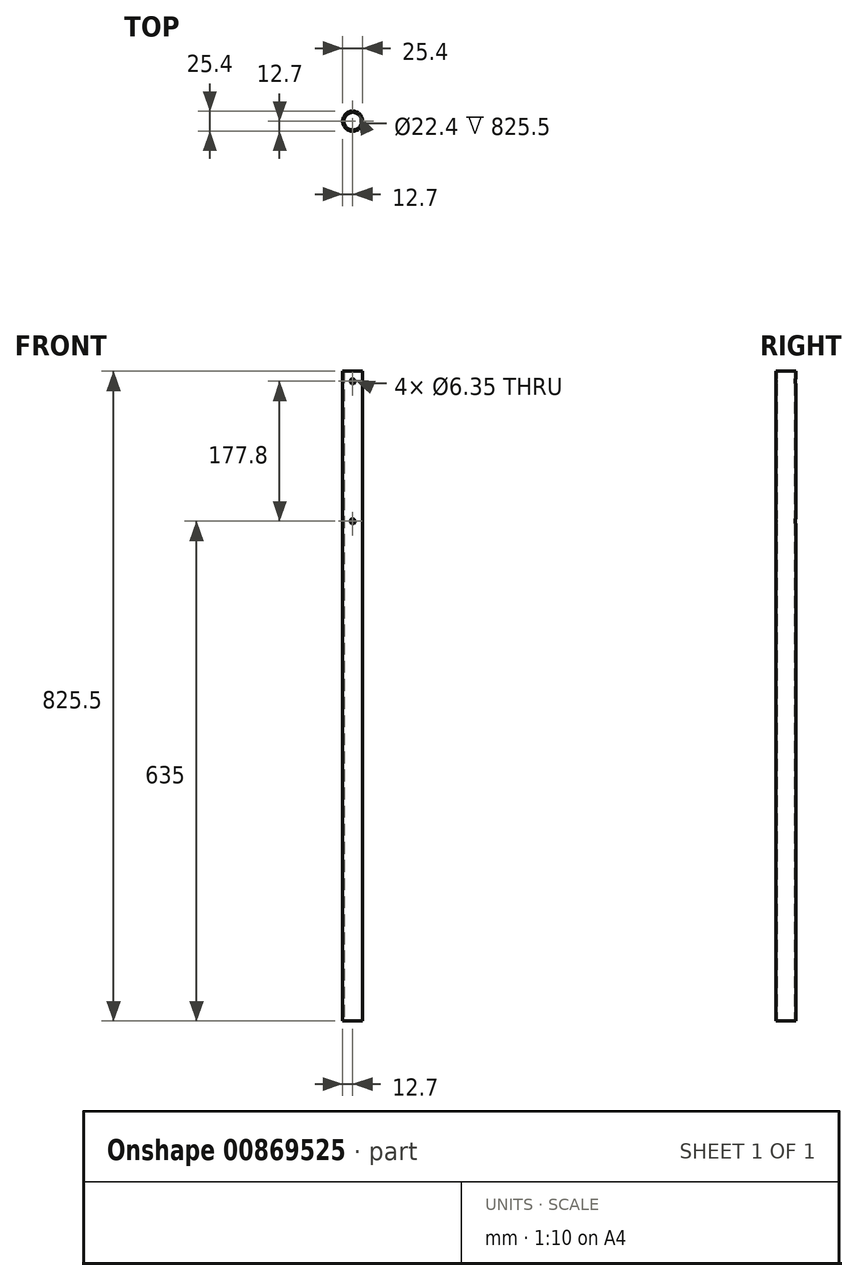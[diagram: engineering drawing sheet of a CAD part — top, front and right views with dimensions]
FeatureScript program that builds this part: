
annotation { "Feature Type Name" : "Feature", "Feature Type Description" : "" }
export const myFeature = defineFeature(function(context is Context, id is Id, definition is map)
    precondition{}
    {
        {
            var Q0;
            Q0=qCreatedBy(makeId("Top.planeOp"),FACE);
            var sketch = newSketch(context, id + "F0", { "sketchPlane" : qUnion([Q0])});
            skCircle(sketch, "E0", {"center": v(0, 0) * mm, "radius": 12.7 * mm});
            skCircle(sketch, "E1.0", {"center": v(0, 0) * mm, "radius": 11.2 * mm});
            skSolve(sketch);
        }
        {
            var Q0;
            Q0 = qSketchRegion(id + "F0", true);
            extrude(context, id + "F1", {"entities" : qUnion([Q0]), "depth" : 825.5 * mm, "offsetDistance" : 25.4 * mm});
        }
        {
            var Q0;
            Q0=qCreatedBy(makeId("Front.planeOp"),FACE);
            var sketch = newSketch(context, id + "F2", { "sketchPlane" : qUnion([Q0])});
            skLineSegment(sketch, "E2", {"start": v(0, 0) * mm, "end": v(0, 825.5) * mm, "construction": true});
            skCircle(sketch, "E3", {"center": v(0, 812.8) * mm, "radius": 3.18 * mm});
            skCircle(sketch, "E4", {"center": v(0, 635) * mm, "radius": 3.17 * mm});
            skSolve(sketch);
        }
        {
            var Q0;
            Q0 = qSketchRegion(id + "F2", true);
            extrude(context, id + "F3", {"entities" : qUnion([Q0]), "operationType" : NewBodyOperationType.REMOVE, "endBound" : BoundingType.SYMMETRIC, "oppositeDirection" : true, "depth" : 25.4 * mm, "offsetDistance" : 25.4 * mm});
        }
    });
